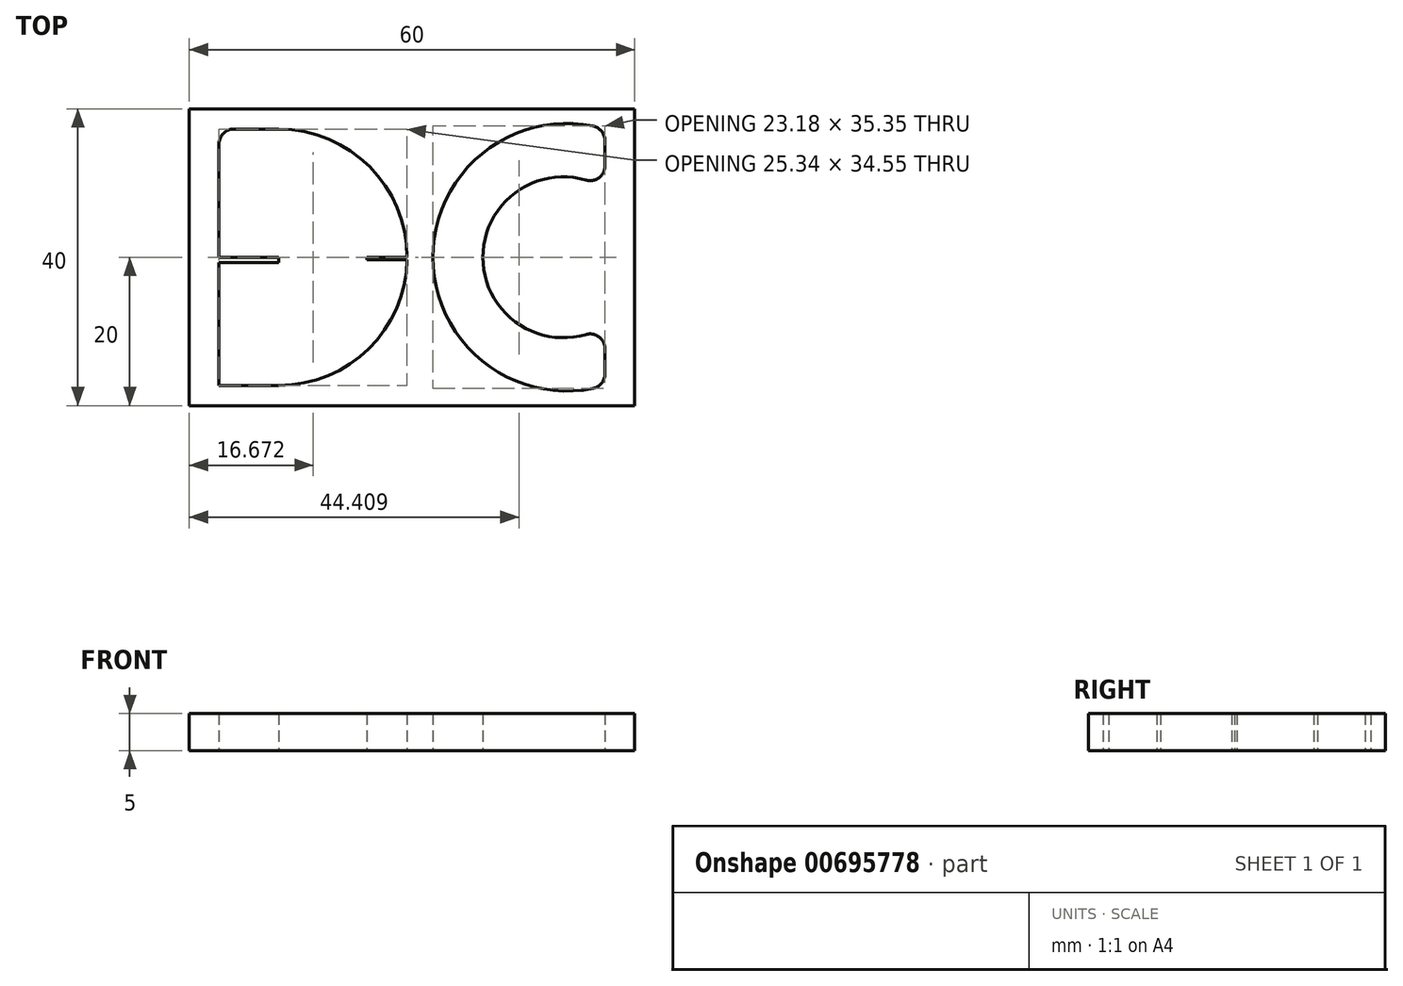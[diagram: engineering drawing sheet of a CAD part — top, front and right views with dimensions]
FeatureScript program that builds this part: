
annotation { "Feature Type Name" : "Feature", "Feature Type Description" : "" }
export const myFeature = defineFeature(function(context is Context, id is Id, definition is map)
    precondition{}
    {
        {
            var Q0;
            Q0=qCreatedBy(makeId("Top.planeOp"),FACE);
            var sketch = newSketch(context, id + "F0", { "sketchPlane" : qUnion([Q0])});
            skLineSegment(sketch, "E0.bottom", {"start": v(-30, -20) * mm, "end": v(30, -20) * mm});
            skLineSegment(sketch, "E0.top", {"start": v(-30, 20) * mm, "end": v(30, 20) * mm});
            skLineSegment(sketch, "E0.left", {"start": v(-30, -20) * mm, "end": v(-30, 20) * mm});
            skLineSegment(sketch, "E0.right", {"start": v(30, -20) * mm, "end": v(30, 20) * mm});
            skPoint(sketch, "E0.middle", {"position": v(0, 0) * mm});
            skLineSegment(sketch, "E1", {"start": v(-33.18, 17.28) * mm, "end": v(39.06, 17.28) * mm, "construction": true});
            skLineSegment(sketch, "E2.MirrorCS", {"start": v(-24, -17.28) * mm, "end": v(39.06, -17.28) * mm, "construction": true});
            skLineSegment(sketch, "E3.bottom", {"start": v(-24, 17.28) * mm, "end": v(-17.93, 17.28) * mm});
            skLineSegment(sketch, "E3.top", {"start": v(-26, -17.28) * mm, "end": v(-17.93, -17.28) * mm});
            skLineSegment(sketch, "E3.left", {"start": v(-26, 15.28) * mm, "end": v(-26, -17.28) * mm});
            skLineSegment(sketch, "E3.right", {"start": v(-17.93, 17.28) * mm, "end": v(-17.93, -17.28) * mm});
            skArc(sketch, "E4", {"start": v(-17.93, -17.28) * mm, "mid": v(-0.66, 0) * mm, "end": v(-17.93, 17.28) * mm});
            skLineSegment(sketch, "E5", {"start": v(-32.9, 9.28) * mm, "end": v(34.34, 9.28) * mm, "construction": true});
            skLineSegment(sketch, "E6.MirrorCS", {"start": v(-32.9, -9.28) * mm, "end": v(34.34, -9.28) * mm, "construction": true});
            skArc(sketch, "E7", {"start": v(-17.93, -9.28) * mm, "mid": v(-6.1, 0) * mm, "end": v(-17.93, 9.28) * mm});
            skLineSegment(sketch, "E8", {"start": v(-26, 23.54) * mm, "end": v(-26, -15.28) * mm, "construction": true});
            skLineSegment(sketch, "E9.MirrorCS", {"start": v(26, 15.72) * mm, "end": v(26, -27.65) * mm, "construction": true});
            skArc(sketch, "E10", {"start": v(24.4, 17.68) * mm, "mid": v(2.82, 0) * mm, "end": v(24.4, -17.68) * mm});
            skArc(sketch, "E11", {"start": v(23.44, 10.4) * mm, "mid": v(9.55, 0) * mm, "end": v(23.44, -10.4) * mm});
            skLineSegment(sketch, "E12", {"start": v(26, 17.28) * mm, "end": v(26, 12.32) * mm});
            skLineSegment(sketch, "E13", {"start": v(26, -12.32) * mm, "end": v(26, -15.72) * mm});
            skPoint(sketch, "E14.newPointA", {"position": v(26, 23.54) * mm});
            skArc(sketch, "E14.filletArc", {"start": v(26, 15.72) * mm, "mid": v(25.55, 16.98) * mm, "end": v(24.4, 17.68) * mm});
            skPoint(sketch, "E15.visualSharp", {"position": v(26, 9.28) * mm});
            skArc(sketch, "E15.filletArc", {"start": v(23.44, 10.4) * mm, "mid": v(25.2, 10.72) * mm, "end": v(26, 12.32) * mm});
            skPoint(sketch, "E16.visualSharp", {"position": v(26, -9.28) * mm});
            skArc(sketch, "E16.filletArc", {"start": v(26, -12.32) * mm, "mid": v(25.2, -10.72) * mm, "end": v(23.44, -10.4) * mm});
            skPoint(sketch, "E17.visualSharp", {"position": v(26, -17.28) * mm});
            skArc(sketch, "E17.filletArc", {"start": v(24.4, -17.68) * mm, "mid": v(25.55, -16.98) * mm, "end": v(26, -15.72) * mm});
            skPoint(sketch, "E18.visualSharp", {"position": v(-26, 17.28) * mm});
            skArc(sketch, "E18.filletArc", {"start": v(-24, 17.28) * mm, "mid": v(-25.41, 16.7) * mm, "end": v(-26, 15.28) * mm});
            skPoint(sketch, "E19.newPointA", {"position": v(-33.18, -17.28) * mm});
            skPoint(sketch, "E19.newPointB", {"position": v(-26, -27.65) * mm});
            skArc(sketch, "E19.filletArc", {"start": v(-26, -15.28) * mm, "mid": v(-25.41, -16.7) * mm, "end": v(-24, -17.28) * mm, "construction": true});
            skLineSegment(sketch, "E20.bottom", {"start": v(-26, 0) * mm, "end": v(-17.93, 0) * mm});
            skLineSegment(sketch, "E20.top", {"start": v(-26, -0.7) * mm, "end": v(-17.93, -0.7) * mm});
            skLineSegment(sketch, "E20.left", {"start": v(-26, 0) * mm, "end": v(-26, -0.7) * mm});
            skLineSegment(sketch, "E20.right", {"start": v(-17.93, 0) * mm, "end": v(-17.93, -0.7) * mm});
            skLineSegment(sketch, "E21", {"start": v(-6.1, 0) * mm, "end": v(-0.66, 0) * mm});
            skLineSegment(sketch, "E22", {"start": v(-6.1, -0.31) * mm, "end": v(-0.66, -0.31) * mm});
            skSolve(sketch);
        }
        {
            var Q0;
            Q0=makeQuery(id+"F0.imprint","IMPRINT",FACE,{"disambiguationData":[TD([[makeQuery(id+"F0.imprint","IMPRINT",EDGE,{"derivedFrom":sQuery(id+"F0.wireOp",EDGE,"E0.bottom")}),1.0]])]});
            var Q1;
            {var subQ5=sQuery(id+"F0.wireOp",EDGE,"E20.right");Q1=makeQuery(id+"F0.imprint","IMPRINT",FACE,{"disambiguationData":[TD([[makeQuery(id+"F0.imprint","IMPRINT",EDGE,{"derivedFrom":subQ5}),1.0]])]});}
            var Q2;
            {var subQ0=sQuery(id+"F0.wireOp",EDGE,"E21");Q2=makeQuery(id+"F0.imprint","IMPRINT",FACE,{"disambiguationData":[TD([[makeQuery(id+"F0.imprint","IMPRINT",EDGE,{"derivedFrom":subQ0}),-1.0]])]});}
            var Q3;
            Q3=makeQuery(id+"F0.imprint","IMPRINT",FACE,{"disambiguationData":[TD([[makeQuery(id+"F0.imprint","IMPRINT",EDGE,{"derivedFrom":sQuery(id+"F0.wireOp",EDGE,"E20.bottom")}),-1.0]])]});
            extrude(context, id + "F1", {"entities" : qUnion([Q0, Q1, Q2, Q3]), "depth" : 5 * mm});
        }
    });
